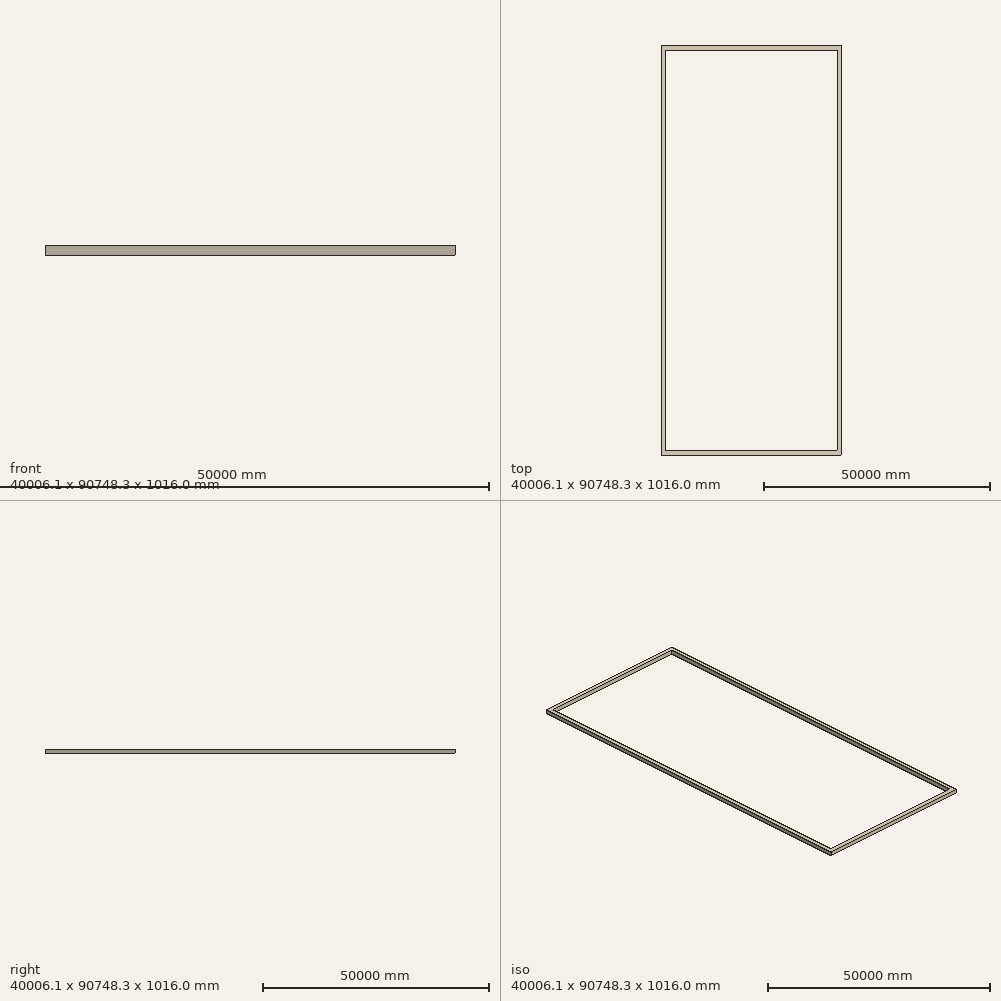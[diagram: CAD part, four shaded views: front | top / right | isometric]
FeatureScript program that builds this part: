
annotation { "Feature Type Name" : "Feature", "Feature Type Description" : "" }
export const myFeature = defineFeature(function(context is Context, id is Id, definition is map)
    precondition{}
    {
        {
            var Q0;
            Q0=qCreatedBy(makeId("Top.planeOp"),FACE);
            var sketch = newSketch(context, id + "F0", { "sketchPlane" : qUnion([Q0])});
            skLineSegment(sketch, "E0.bottom", {"start": v(18987.07, 44358.17) * mm, "end": v(-18987.07, 44358.17) * mm});
            skLineSegment(sketch, "E0.top", {"start": v(18987.07, -44358.17) * mm, "end": v(-18987.07, -44358.17) * mm});
            skLineSegment(sketch, "E0.left", {"start": v(18987.07, 44358.17) * mm, "end": v(18987.07, -44358.17) * mm});
            skLineSegment(sketch, "E0.right", {"start": v(-18987.07, 44358.17) * mm, "end": v(-18987.07, -44358.17) * mm});
            skPoint(sketch, "E0.middle", {"position": v(0, 0) * mm});
            skLineSegment(sketch, "E1.0", {"start": v(-20003.07, 45374.17) * mm, "end": v(-20003.07, -45374.17) * mm});
            skLineSegment(sketch, "E1.1", {"start": v(20003.07, 45374.17) * mm, "end": v(-20003.07, 45374.17) * mm});
            skLineSegment(sketch, "E1.2", {"start": v(20003.07, 45374.17) * mm, "end": v(20003.07, -45374.17) * mm});
            skLineSegment(sketch, "E1.3", {"start": v(20003.07, -45374.17) * mm, "end": v(-20003.07, -45374.17) * mm});
            skSolve(sketch);
        }
        {
            var Q0;
            Q0 = qSketchRegion(id + "F0", true);
            extrude(context, id + "F1", {"entities" : qUnion([Q0]), "depth" : 1016 * mm, "offsetDistance" : 25.4 * mm});
        }
    });
